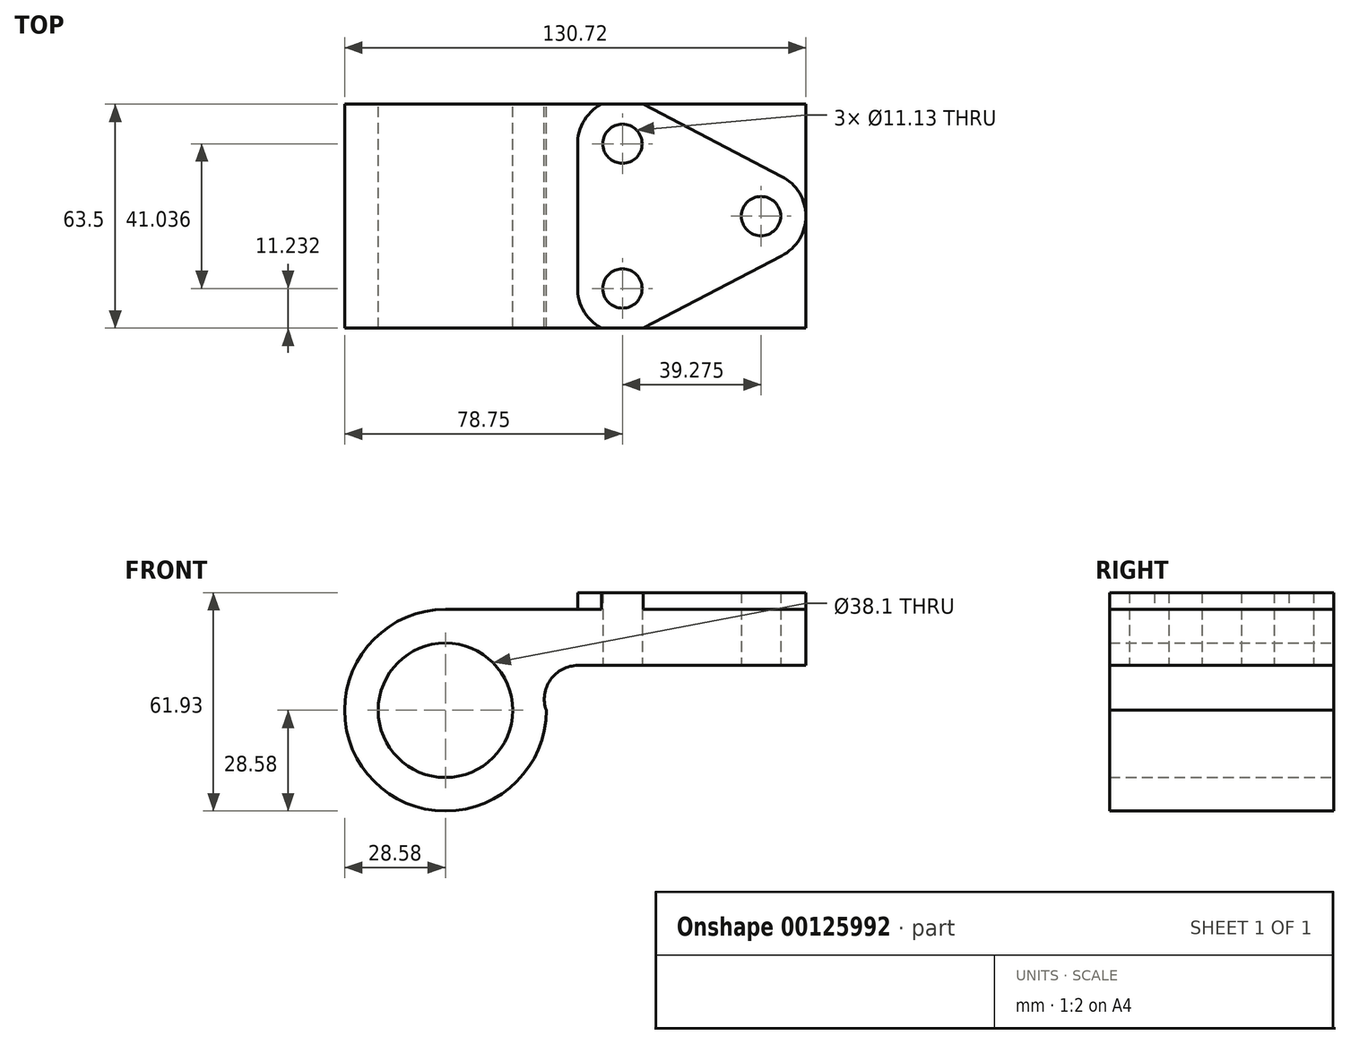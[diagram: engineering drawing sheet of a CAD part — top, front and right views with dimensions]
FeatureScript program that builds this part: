
annotation { "Feature Type Name" : "Feature", "Feature Type Description" : "" }
export const myFeature = defineFeature(function(context is Context, id is Id, definition is map)
    precondition{}
    {
        {
            var Q0;
            Q0=qCreatedBy(makeId("Front.planeOp"),FACE);
            var sketch = newSketch(context, id + "F0", { "sketchPlane" : qUnion([Q0])});
            skCircle(sketch, "E0", {"center": v(0, 0) * mm, "radius": 19.05 * mm});
            skLineSegment(sketch, "E1", {"start": v(0, 28.58) * mm, "end": v(102.14, 28.58) * mm});
            skLineSegment(sketch, "E2", {"start": v(102.14, 28.58) * mm, "end": v(102.14, 12.7) * mm});
            skLineSegment(sketch, "E3", {"start": v(0, 0) * mm, "end": v(57.15, 0) * mm, "construction": true});
            skLineSegment(sketch, "E4", {"start": v(102.14, 12.7) * mm, "end": v(37.56, 12.7) * mm});
            skArc(sketch, "E5", {"start": v(37.56, 12.7) * mm, "mid": v(29.78, 8.67) * mm, "end": v(28.58, 0) * mm});
            skArc(sketch, "E6", {"start": v(0, 28.58) * mm, "mid": v(-20.2, -20.2) * mm, "end": v(28.58, 0) * mm});
            skPoint(sketch, "E7", {"position": v(69.85, 12.7) * mm});
            skSolve(sketch);
        }
        {
            var Q0;
            Q0 = qSketchRegion(id + "F0", true);
            extrude(context, id + "F1", {"entities" : qUnion([Q0]), "endBound" : BoundingType.SYMMETRIC, "depth" : 63.5 * mm});
        }
        {
            var Q0;
            Q0=makeQuery(id+"F1.opExtrude","CAP_FACE",FACE,{"disambiguationData":[OSD([sQuery(id+"F0.wireOp",EDGE,"E0"),sQuery(id+"F0.wireOp",EDGE,"E1"),sQuery(id+"F0.wireOp",EDGE,"E2"),sQuery(id+"F0.wireOp",EDGE,"E4"),sQuery(id+"F0.wireOp",EDGE,"E5"),sQuery(id+"F0.wireOp",EDGE,"E6")])],"isStart":false});
            var sketch = newSketch(context, id + "F2", { "sketchPlane" : qUnion([Q0])});
            skLineSegment(sketch, "E8", {"start": v(37.56, 12.7) * mm, "end": v(37.56, 28.58) * mm, "construction": true});
            skSolve(sketch);
        }
        {
            var Q0;
            Q0=makeQuery(id+"F1.opExtrude","SWEPT_FACE",FACE,{"disambiguationData":[OSD([sQuery(id+"F0.wireOp",EDGE,"E1")])]});
            var sketch = newSketch(context, id + "F3", { "sketchPlane" : qUnion([Q0])});
            skLineSegment(sketch, "E9", {"start": v(37.56, 19.05) * mm, "end": v(37.56, -19.05) * mm});
            skLineSegment(sketch, "E10", {"start": v(56.05, 31.77) * mm, "end": v(95.33, 11.26) * mm});
            skLineSegment(sketch, "E11", {"start": v(95.33, -11.26) * mm, "end": v(56.05, -31.77) * mm});
            skArc(sketch, "E12", {"start": v(56.05, 31.77) * mm, "mid": v(42.97, 30.98) * mm, "end": v(37.56, 19.05) * mm});
            skArc(sketch, "E13", {"start": v(95.33, -11.26) * mm, "mid": v(102.14, 0) * mm, "end": v(95.33, 11.26) * mm});
            skArc(sketch, "E14", {"start": v(37.56, -19.05) * mm, "mid": v(42.97, -30.98) * mm, "end": v(56.05, -31.77) * mm});
            skLineSegment(sketch, "E15", {"start": v(37.56, -19.05) * mm, "end": v(37.56, -31.75) * mm, "construction": true});
            skLineSegment(sketch, "E16", {"start": v(37.56, 19.05) * mm, "end": v(37.56, 31.75) * mm, "construction": true});
            skPoint(sketch, "E17", {"position": v(102.14, 0) * mm});
            skPoint(sketch, "E18", {"position": v(37.56, 0) * mm});
            skLineSegment(sketch, "E19", {"start": v(37.56, 0) * mm, "end": v(102.14, 0) * mm, "construction": true});
            skCircle(sketch, "E20", {"center": v(89.44, 0) * mm, "radius": 5.56 * mm});
            skCircle(sketch, "E21", {"center": v(50.17, 20.52) * mm, "radius": 5.56 * mm});
            skCircle(sketch, "E22", {"center": v(50.17, -20.52) * mm, "radius": 5.56 * mm});
            skSolve(sketch);
        }
        {
            var Q0;
            {var subQ10=sQuery(id+"F3.wireOp",EDGE,"E9");Q0=makeQuery(id+"F3.imprint","IMPRINT",FACE,{"disambiguationData":[TD([[makeQuery(id+"F3.imprint","IMPRINT",EDGE,{"derivedFrom":subQ10}),1.0]])]});}
            extrude(context, id + "F4", {"entities" : qUnion([Q0]), "operationType" : NewBodyOperationType.ADD, "depth" : 4.78 * mm});
        }
        {
            var Q0;
            Q0=makeQuery(id+"F4.boolean.opBoolean","SPLIT",FACE,{"disambiguationData":[TD([makeQuery(id+"F4.opExtrude","SWEPT_FACE",FACE,{"disambiguationData":[OSD([sQuery(id+"F3.wireOp",EDGE,"E20")])]})])],"derivedFrom":makeQuery(id+"F1.opExtrude","SWEPT_FACE",FACE,{"disambiguationData":[OSD([sQuery(id+"F0.wireOp",EDGE,"E1")])]})});
            var Q1;
            Q1=makeQuery(id+"F4.boolean.opBoolean","SPLIT",FACE,{"disambiguationData":[TD([makeQuery(id+"F4.opExtrude","SWEPT_FACE",FACE,{"disambiguationData":[OSD([sQuery(id+"F3.wireOp",EDGE,"E22")])]})])],"derivedFrom":makeQuery(id+"F1.opExtrude","SWEPT_FACE",FACE,{"disambiguationData":[OSD([sQuery(id+"F0.wireOp",EDGE,"E1")])]})});
            var Q2;
            Q2=makeQuery(id+"F4.boolean.opBoolean","SPLIT",FACE,{"disambiguationData":[TD([makeQuery(id+"F4.opExtrude","SWEPT_FACE",FACE,{"disambiguationData":[OSD([sQuery(id+"F3.wireOp",EDGE,"E21")])]})])],"derivedFrom":makeQuery(id+"F1.opExtrude","SWEPT_FACE",FACE,{"disambiguationData":[OSD([sQuery(id+"F0.wireOp",EDGE,"E1")])]})});
            extrude(context, id + "F5", {"entities" : qUnion([Q0, Q1, Q2]), "operationType" : NewBodyOperationType.REMOVE, "endBound" : BoundingType.THROUGH_ALL, "oppositeDirection" : true, "depth" : 25.4 * mm});
        }
    });
